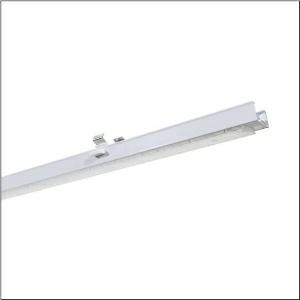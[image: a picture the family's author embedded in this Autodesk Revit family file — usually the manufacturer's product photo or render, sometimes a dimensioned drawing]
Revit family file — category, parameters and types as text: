
# Revit family: trunking_flex_31_51re12ma66b
name_source: partatom
category: Lighting Fixtures
units: mm (PartAtom-declared; Revit-internal decimal feet)

## family parameters
Cut with Voids When Loaded = No
Host = Face
Light Source = No
Part Type = Normal
Room Calculation Point = No
Round Connector Dimension = Use Diameter
Shared = No

## types (1)
- --- (1 x LED, 6400 lm, 40 W, 6500K)
    Apparent Load = 40 VA
    CIE Flux Codes = 65 91 98 99 100
    Color Rendering = 80
    Color Temperature = 6500K
    Default Elevation = 1800 mm
    Description = Trunking Flex 31, luminaire insert, of extruded aluminium section, coated, traffic white (RAL 9016), length: 1.172mm, width: 91mm, height: 53mm, LED rated luminous flux: 6.400lm, light colour: 865, control gear: ON/OFF Multilumen, with system connector: socket, mains connection: 220..240V, AC, 50/60Hz, rated input power: 40W, luminous flux adjustable on luminaire in four steps (3420/4540/5580/6630lm), connected load according to luminous flux setting (20/26/33/40W), primary light control with lens, of plastic, primary optical cover: cover, of PMMA, light emission: direct distribution, protection rating (complete): IP20, insulation class (complete): insulation class I (protective earthing), certification: CE, UKCA, impact resistance: IK02, permissible ambient temperature for indoor applications: -20..+40°C, packaging unit: 1 piece
    Height = 58 mm
    Lamp = 1 x LED
    Lamp Light Flux = 6400 lm
    Lamp Power = 40 W
    Lamp count = 1
    Length = 1172 mm
    Luminous efficacy = 160 lm/W
    Manufacturer = Siteco
    ModVariant = No
    Model = 51RE12MA66B
    Mounting Place = Ceiling
    Mounting Type = Pendant
    Number of Poles = 1
    OnlyDefault = Yes
    Power Factor = 1
    Product Name = Trunking Flex 31
    Product group = luminaire insert
    ProductGroupID = 902
    Protection Class = Protection class I
    Protection Degree = IP 20
    RLX_Detail_Level = 1
    RLX_Emergency_Light_Flux = 0 lm
    RLX_Emergency_Type = 0
    RLX_Emergency_Type_DB = No
    RlxData = <blob elided: 19969 chars, md5=a44549c0>
    Socket = socket
    Standby Power = 0 W
    System Light Flux = 6400 lm
    System Power = 40 W
    Type Comments = factory setting: luminous flux: 100 % | (ON | ON) | 300 mA
    Type Image = l_1266702.jpg
    URL = http://relux.com
    VarID = @adj_059182
    Voltage = 0 V
    Weight = 0.00 kg
    Width = 65 mm

## geometry (parser evidence)
native form markers: Blend x4, Sweep x13
no freeform markers — native parametric forms only
